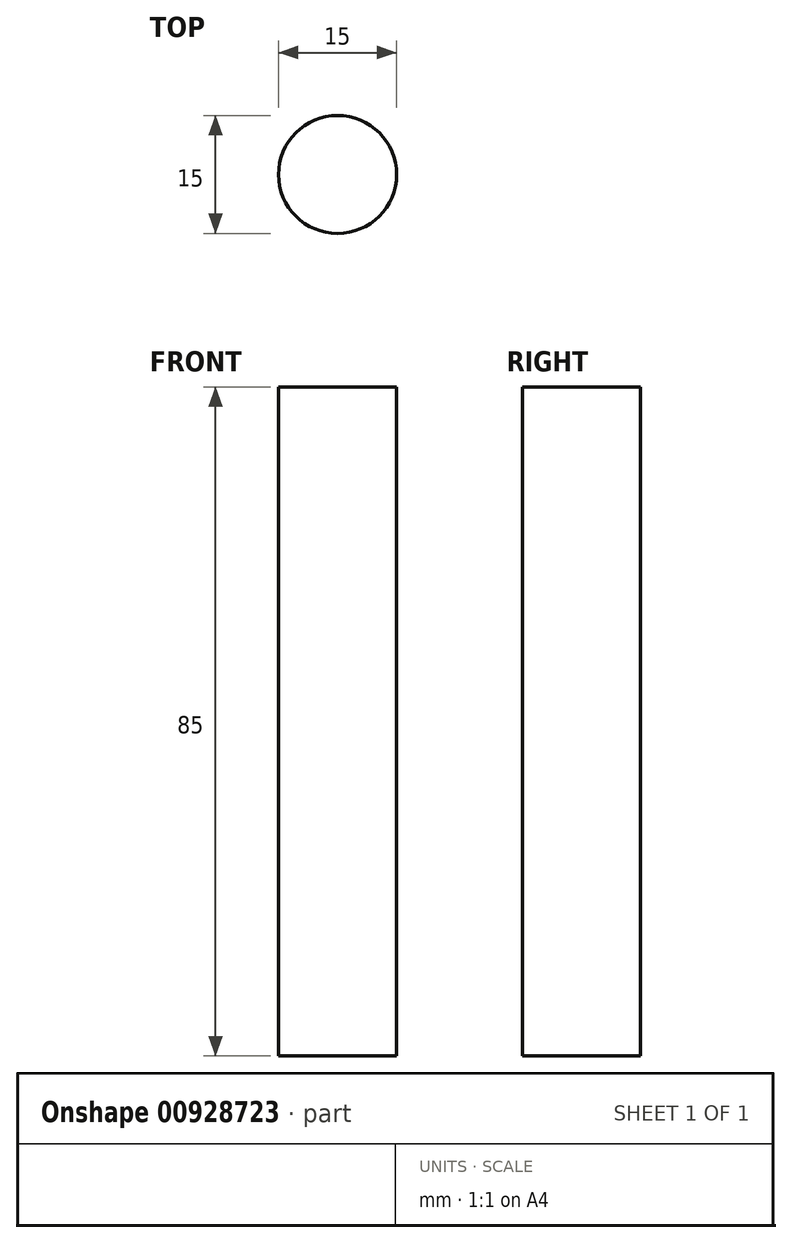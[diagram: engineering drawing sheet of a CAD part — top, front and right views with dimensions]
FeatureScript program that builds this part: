
annotation { "Feature Type Name" : "Feature", "Feature Type Description" : "" }
export const myFeature = defineFeature(function(context is Context, id is Id, definition is map)
    precondition{}
    {
        {
            var Q0;
            Q0=qCreatedBy(makeId("Front.planeOp"),FACE);
            var sketch = newSketch(context, id + "F0", { "sketchPlane" : qUnion([Q0])});
            skLineSegment(sketch, "E0.bottom", {"start": v(7.5, 12.5) * mm, "end": v(-7.5, 12.5) * mm});
            skLineSegment(sketch, "E0.top", {"start": v(7.5, -12.5) * mm, "end": v(-7.5, -12.5) * mm});
            skLineSegment(sketch, "E0.left", {"start": v(7.5, 12.5) * mm, "end": v(7.5, -12.5) * mm});
            skLineSegment(sketch, "E0.right", {"start": v(-7.5, 12.5) * mm, "end": v(-7.5, -12.5) * mm});
            skPoint(sketch, "E0.middle", {"position": v(0, 0) * mm});
            skPoint(sketch, "E1.middle", {"position": v(7.5, 12.5) * mm});
            skLineSegment(sketch, "E2.bottom", {"start": v(-7.5, 12.5) * mm, "end": v(7.5, 12.5) * mm});
            skLineSegment(sketch, "E2.top", {"start": v(-7.5, 47.5) * mm, "end": v(7.5, 47.5) * mm});
            skLineSegment(sketch, "E2.left", {"start": v(-7.5, 12.5) * mm, "end": v(-7.5, 47.5) * mm});
            skLineSegment(sketch, "E2.right", {"start": v(7.5, 12.5) * mm, "end": v(7.5, 47.5) * mm});
            skLineSegment(sketch, "E3.top", {"start": v(-7.5, 72.5) * mm, "end": v(7.5, 72.5) * mm});
            skLineSegment(sketch, "E3.left", {"start": v(-7.5, 47.5) * mm, "end": v(-7.5, 72.5) * mm});
            skLineSegment(sketch, "E3.right", {"start": v(7.5, 47.5) * mm, "end": v(7.5, 72.5) * mm});
            skArc(sketch, "E4", {"start": v(7.5, 72.5) * mm, "mid": v(0, 75.89) * mm, "end": v(-7.5, 72.5) * mm});
            skLineSegment(sketch, "E5", {"start": v(0, 0) * mm, "end": v(0, 72.5) * mm});
            skSolve(sketch);
        }
        {
            var Q0;
            Q0=makeQuery(id+"F0.imprint","IMPRINT",FACE,{"disambiguationData":[TD([[makeQuery(id+"F0.imprint","IMPRINT",EDGE,{"derivedFrom":sQuery(id+"F0.wireOp",EDGE,"E0.bottom")}),1.0]])]});
            var Q1;
            Q1=makeQuery(id+"F0.imprint","IMPRINT",FACE,{"disambiguationData":[TD([[makeQuery(id+"F0.imprint","IMPRINT",EDGE,{"derivedFrom":sQuery(id+"F0.wireOp",EDGE,"E0.top")}),-1.0]])]});
            var Q2;
            {var subQ0=sQuery(id+"F0.wireOp",EDGE,"E2.right");Q2=makeQuery(id+"F0.imprint","IMPRINT",FACE,{"disambiguationData":[TD([[makeQuery(id+"F0.imprint","IMPRINT",EDGE,{"derivedFrom":subQ0}),1.0]])]});}
            var Q3;
            {var subQ0=sQuery(id+"F0.wireOp",EDGE,"E3.left");Q3=makeQuery(id+"F0.imprint","IMPRINT",FACE,{"disambiguationData":[TD([[makeQuery(id+"F0.imprint","IMPRINT",EDGE,{"derivedFrom":subQ0}),-1.0]])]});}
            var Q4;
            {var subQ0=sQuery(id+"F0.wireOp",EDGE,"E3.right");Q4=makeQuery(id+"F0.imprint","IMPRINT",FACE,{"disambiguationData":[TD([[makeQuery(id+"F0.imprint","IMPRINT",EDGE,{"derivedFrom":subQ0}),1.0]])]});}
            var Q5;
            {var subQ0=sQuery(id+"F0.wireOp",EDGE,"E2.left");Q5=makeQuery(id+"F0.imprint","IMPRINT",FACE,{"disambiguationData":[TD([[makeQuery(id+"F0.imprint","IMPRINT",EDGE,{"derivedFrom":subQ0}),-1.0]])]});}
            extrude(context, id + "F1", {"entities" : qUnion([Q0, Q1, Q2, Q3, Q4, Q5]), "depth" : 7.5 * mm, "offsetDistance" : 25 * mm, "hasSecondDirection" : true, "secondDirectionOppositeDirection" : true, "secondDirectionDepth" : 7.5 * mm});
        }
        {
            var Q0;
            Q0=makeQuery(id+"F1.opExtrude","CAP_EDGE",EDGE,{"disambiguationData":[OSD([sQuery(id+"F0.wireOp",EDGE,"E0.right")])],"isStart":false});
            var Q1;
            Q1=makeQuery(id+"F1.opExtrude","CAP_EDGE",EDGE,{"disambiguationData":[OSD([sQuery(id+"F0.wireOp",EDGE,"E0.left")])],"isStart":false});
            var Q2;
            Q2=makeQuery(id+"F1.opExtrude","CAP_EDGE",EDGE,{"disambiguationData":[OSD([sQuery(id+"F0.wireOp",EDGE,"E0.right")])],"isStart":true});
            var Q3;
            Q3=makeQuery(id+"F1.opExtrude","CAP_EDGE",EDGE,{"disambiguationData":[OSD([sQuery(id+"F0.wireOp",EDGE,"E0.left")])],"isStart":true});
            fillet(context, id + "F2", {"entities" : qUnion([Q0, Q1, Q2, Q3]), "radius" : 7.5 * mm, "tangentPropagation" : true, "allowEdgeOverflow" : false});
        }
    });
